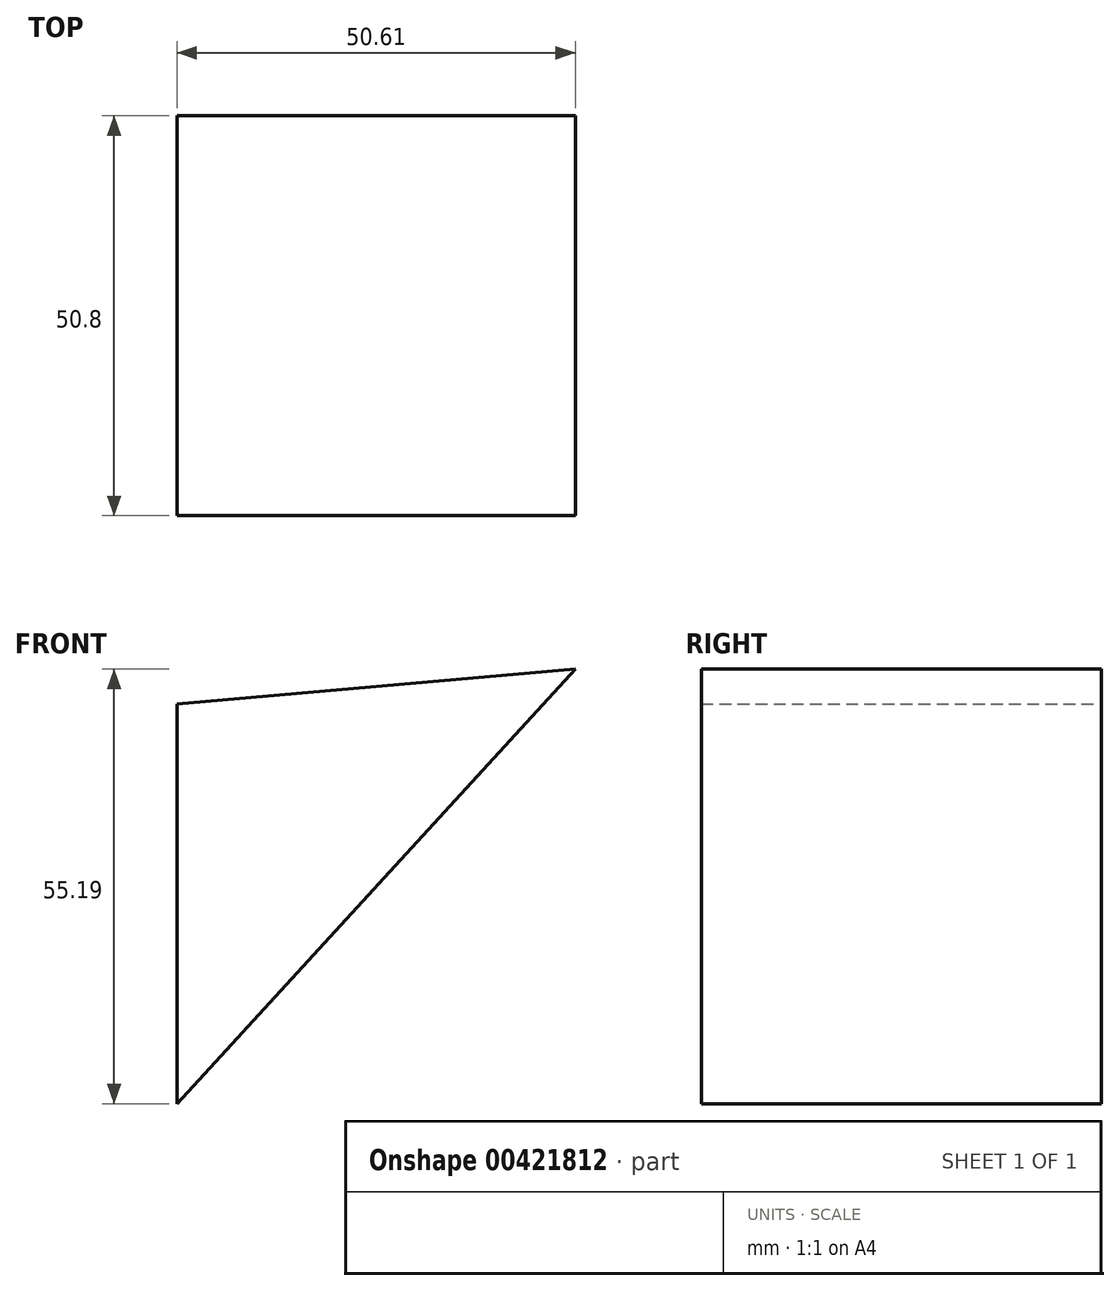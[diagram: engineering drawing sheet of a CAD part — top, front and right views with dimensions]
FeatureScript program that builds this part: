
annotation { "Feature Type Name" : "Feature", "Feature Type Description" : "" }
export const myFeature = defineFeature(function(context is Context, id is Id, definition is map)
    precondition{}
    {
        {
            var Q0;
            Q0=qCreatedBy(makeId("Front.planeOp"),FACE);
            var sketch = newSketch(context, id + "F0", { "sketchPlane" : qUnion([Q0])});
            skLineSegment(sketch, "E0", {"start": v(0, 0) * mm, "end": v(0, 50.8) * mm});
            skLineSegment(sketch, "E1", {"start": v(0, 50.8) * mm, "end": v(50.6, 55.2) * mm});
            skLineSegment(sketch, "E2", {"start": v(50.6, 55.2) * mm, "end": v(0, 0) * mm});
            skSolve(sketch);
        }
        {
            var Q0;
            Q0 = qSketchRegion(id + "F0", true);
            extrude(context, id + "F1", {"entities" : qUnion([Q0]), "depth" : 50.8 * mm});
        }
    });
